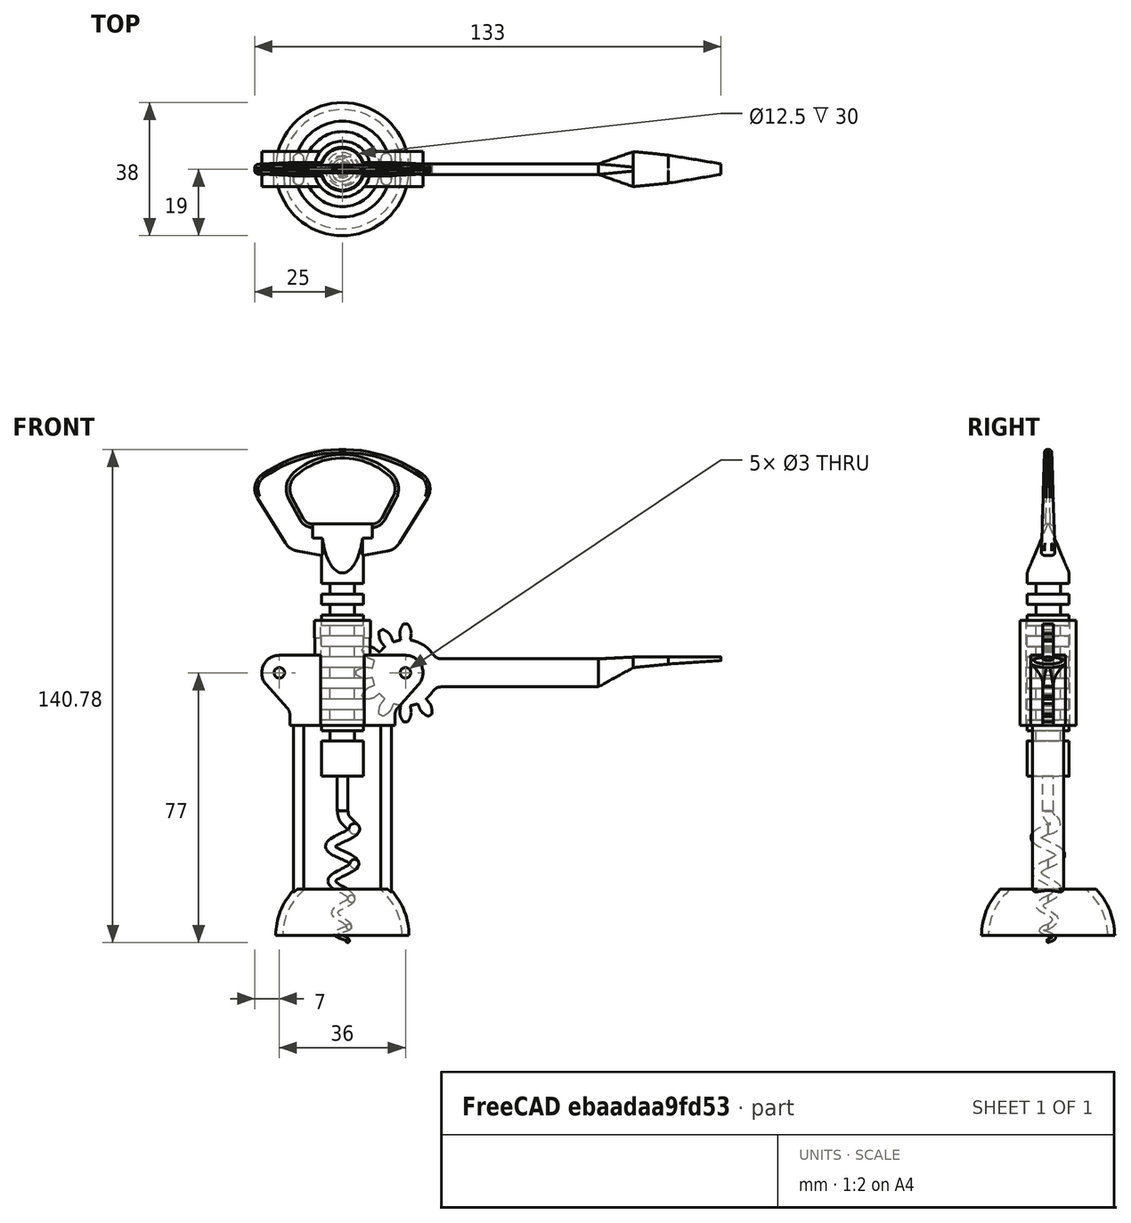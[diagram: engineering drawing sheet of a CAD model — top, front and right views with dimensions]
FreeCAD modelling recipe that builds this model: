
FCSTD DOCUMENT  (FreeCAD 0.18R13524 (Git))
Label: SACA ROLHAS - CJ
License: All rights reserved
LicenseURL: http://en.wikipedia.org/wiki/All_rights_reserved
objects: App::FeaturePython×6, Part::FeaturePython×4
note: 4 computed .brp shape members not serialized (recipe doc carries the construction recipe); baked Part::Feature solids carry a one-line shape summary decoded from their .brp

FEATURE [Part::FeaturePython] SACA_ROLHAS___CORPO_01  # a2plus imported part (geometry in sourceFile) (typed FeaturePython)
  fixedPosition = true
  sourceFile = <path> SACA ROLHAS - CORKSCREWS/SACA ROLHAS - CORPO.FCStd
  timeLastImport = 1.52492e+09
  updateColors = true
FEATURE [Part::FeaturePython] SACA_ROLHAS___MOLA_01  # a2plus imported part (geometry in sourceFile) (typed FeaturePython)
  Placement = pos=(0,0,-61.5) rot=(0,0,1;0rad)
  fixedPosition = false
  sourceFile = <path> SACA ROLHAS - CORKSCREWS/SACA ROLHAS - MOLA.FCStd
  timeLastImport = 1.52492e+09
  updateColors = true
FEATURE [App::FeaturePython] circularEdgeConstraint01  label="circularEdgeConstraint01__SACA_ROLHAS___CORPO_01"  # a2plus constraint (typed FeaturePython)
  Object1 = SACA_ROLHAS___MOLA_01
  Object2 = SACA_ROLHAS___CORPO_01
  SubElement1 = Edge75
  SubElement2 = Edge123
  Type = circularEdge
  directionConstraint = 0
  lockRotation = false
  offset = 10.5
FEATURE [App::FeaturePython] circularEdgeConstraint01_mirror  label="circularEdgeConstraint01__SACA_ROLHAS___MOLA_01"  # a2plus constraint (typed FeaturePython)
  Object1 = SACA_ROLHAS___MOLA_01
  Object2 = SACA_ROLHAS___CORPO_01
  SubElement1 = Edge75
  SubElement2 = Edge123
  Type = circularEdge
  directionConstraint = 0
  lockRotation = false
  offset = 10.5
FEATURE [Part::FeaturePython] SACA_ROLHAS___ENGRENAGEM_01  # a2plus imported part (geometry in sourceFile) (typed FeaturePython)
  Placement = pos=(-18,1.5,15) rot=(-0.57735,-0.57735,0.57735;4.18879rad)
  fixedPosition = false
  sourceFile = <path> SACA ROLHAS - CORKSCREWS/SACA ROLHAS - ENGRENAGEM.FCStd
  timeLastImport = 1.52492e+09
  updateColors = true
FEATURE [App::FeaturePython] circularEdgeConstraint02  label="circularEdgeConstraint02__SACA_ROLHAS___CORPO_01"  # a2plus constraint (typed FeaturePython)
  Object1 = SACA_ROLHAS___ENGRENAGEM_01
  Object2 = SACA_ROLHAS___CORPO_01
  SubElement1 = Edge91
  SubElement2 = Edge147
  Type = circularEdge
  directionConstraint = 1
  lockRotation = false
  offset = 0
FEATURE [App::FeaturePython] circularEdgeConstraint02_mirror  label="circularEdgeConstraint02__SACA_ROLHAS___ENGRENAGEM_01"  # a2plus constraint (typed FeaturePython)
  Object1 = SACA_ROLHAS___ENGRENAGEM_01
  Object2 = SACA_ROLHAS___CORPO_01
  SubElement1 = Edge91
  SubElement2 = Edge147
  Type = circularEdge
  directionConstraint = 1
  lockRotation = false
  offset = 0
FEATURE [Part::FeaturePython] Clone  label="SACA_ROLHAS___ENGRENAGEM_002"  # Draft clone (typed FeaturePython)
  AttacherType = Attacher::AttachEngine3D
  Fuse = false
  Objects = -> [SACA_ROLHAS___ENGRENAGEM_01]
  Placement = pos=(18,-1.5,15) rot=(-0.57735,0.57735,0.57735;2.0944rad)
  Scale = (1,1,1)
FEATURE [App::FeaturePython] circularEdgeConstraint03  label="circularEdgeConstraint03__SACA_ROLHAS___CORPO_01"  # a2plus constraint (typed FeaturePython)
  Object1 = Clone
  Object2 = SACA_ROLHAS___CORPO_01
  SubElement1 = Edge150
  SubElement2 = Edge140
  Type = circularEdge
  directionConstraint = 0
  lockRotation = false
  offset = 0
FEATURE [App::FeaturePython] circularEdgeConstraint03_mirror  label="circularEdgeConstraint03__SACA_ROLHAS___ENGRENAGEM_002"  # a2plus constraint (typed FeaturePython)
  Object1 = Clone
  Object2 = SACA_ROLHAS___CORPO_01
  SubElement1 = Edge150
  SubElement2 = Edge140
  Type = circularEdge
  directionConstraint = 0
  lockRotation = false
  offset = 0
note: 3 file-system paths scrubbed to <path> (originals preserved in the JSON sidecar)
